# Revit family: Healthcare-Hill_Rom-Progressa
name_source: partatom
category: Specialty Equipment
revit_build: Autodesk Revit Architecture 2013 (Build: 20130531_2115(x64)
units: mm (PartAtom-declared; Revit-internal decimal feet)

## types (1)
- Progressa
    Actual Foot Angle = 0.25°
    Actual Head Angle = 0.25°
    Assembly Code = E1020810
    Bumpers = Plastic-Hill-Rom-Light Blue
    Description = Full Featured Hospital Bed
    Finish = Plastic-Hill-Rom-Light Beige
    Foot Angle = 0.00°
    Head Angle = 0.00°
    Height = 2' - 11"
    Length = 7' - 4"
    Manufacturer = Hill-Rom Co.
    Mattress = Textile-Hill Rom-Matress
    Mattress Height = 0' - 6"
    Model = Progressa Bed System
    Product Documentation Link = http://www.hill-rom.com
    Product Name = Progressa
    Type Comments = ICU Bed System
    URL = www.hill-rom.com
    Wheels = Plastic-Hill-Rom-Light Blue
    Width = 3' - 4 1/2"

## geometry (parser evidence)
native form markers: Blend x34, Sweep x17
no freeform markers — native parametric forms only
